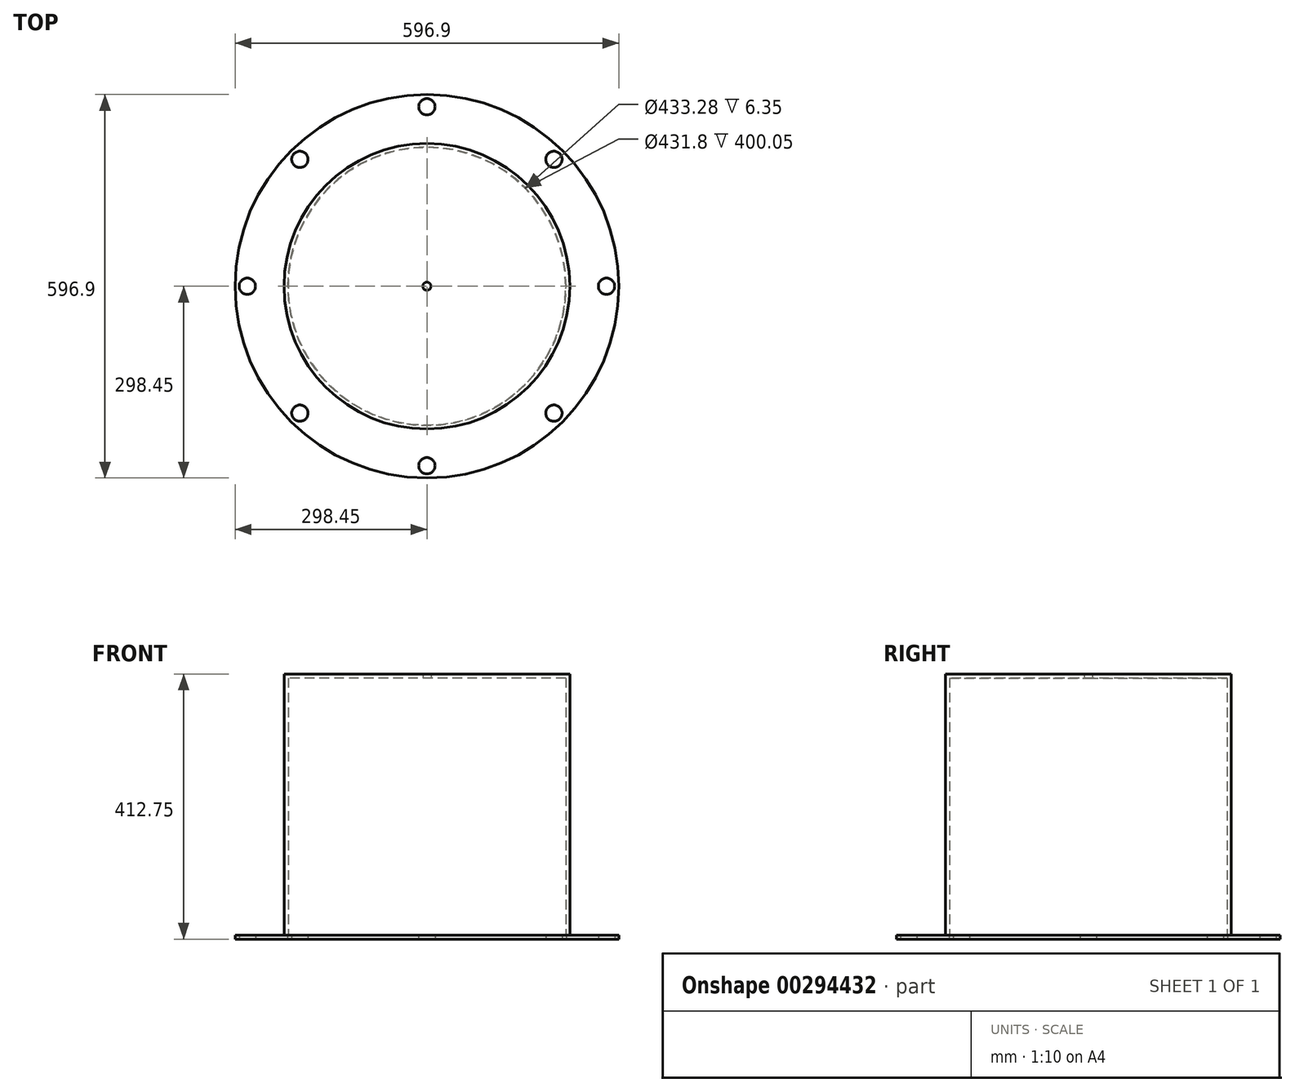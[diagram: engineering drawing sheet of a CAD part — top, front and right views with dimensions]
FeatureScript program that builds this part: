
annotation { "Feature Type Name" : "Feature", "Feature Type Description" : "" }
export const myFeature = defineFeature(function(context is Context, id is Id, definition is map)
    precondition{}
    {
        {
            var Q0;
            Q0=qCreatedBy(makeId("Top.planeOp"),FACE);
            var sketch = newSketch(context, id + "F0", { "sketchPlane" : qUnion([Q0])});
            skCircle(sketch, "E0", {"center": v(0, 0) * mm, "radius": 298.45 * mm});
            skCircle(sketch, "E1", {"center": v(0, 0) * mm, "radius": 216.64 * mm});
            skCircle(sketch, "E2", {"center": v(0, 279.4) * mm, "radius": 12.7 * mm});
            skCircle(sketch, "E3.1.0", {"center": v(-197.57, 197.57) * mm, "radius": 12.7 * mm});
            skCircle(sketch, "E3.2.0", {"center": v(-279.4, 0) * mm, "radius": 12.7 * mm});
            skCircle(sketch, "E3.3.0", {"center": v(-197.57, -197.57) * mm, "radius": 12.7 * mm});
            skCircle(sketch, "E3.4.0", {"center": v(0, -279.4) * mm, "radius": 12.7 * mm});
            skCircle(sketch, "E3.5.0", {"center": v(197.57, -197.57) * mm, "radius": 12.7 * mm});
            skCircle(sketch, "E3.6.0", {"center": v(279.4, 0) * mm, "radius": 12.7 * mm});
            skCircle(sketch, "E3.7.0", {"center": v(197.57, 197.57) * mm, "radius": 12.7 * mm});
            skSolve(sketch);
        }
        {
            var Q0;
            Q0=makeQuery(id+"F0.imprint","IMPRINT",FACE,{"disambiguationData":[TD([[makeQuery(id+"F0.imprint","IMPRINT",EDGE,{"derivedFrom":sQuery(id+"F0.wireOp",EDGE,"E0")}),1.0]])]});
            extrude(context, id + "F1", {"entities" : qUnion([Q0]), "depth" : 6.35 * mm});
        }
        {
            var Q0;
            Q0=makeQuery(id+"F1.opExtrude","CAP_FACE",FACE,{"disambiguationData":[OSD([sQuery(id+"F0.wireOp",EDGE,"E0"),sQuery(id+"F0.wireOp",EDGE,"E1"),sQuery(id+"F0.wireOp",EDGE,"E2"),sQuery(id+"F0.wireOp",EDGE,"E3.1.0"),sQuery(id+"F0.wireOp",EDGE,"E3.2.0"),sQuery(id+"F0.wireOp",EDGE,"E3.3.0"),sQuery(id+"F0.wireOp",EDGE,"E3.4.0"),sQuery(id+"F0.wireOp",EDGE,"E3.5.0"),sQuery(id+"F0.wireOp",EDGE,"E3.6.0"),sQuery(id+"F0.wireOp",EDGE,"E3.7.0")])],"isStart":false});
            cPlane(context, id + "F2", {"entities" : qUnion([Q0]), "cplaneType" : CPlaneType.OFFSET, "offset" : 0 * mm, "width" : 152.4 * mm, "height" : 152.4 * mm});
        }
        {
            var Q0;
            Q0=qCreatedBy(id+"F2.planeOp",FACE);
            var sketch = newSketch(context, id + "F3", { "sketchPlane" : qUnion([Q0])});
            skCircle(sketch, "E4", {"center": v(0, 0) * mm, "radius": 215.9 * mm});
            skCircle(sketch, "E5", {"center": v(0, 0) * mm, "radius": 222.25 * mm});
            skSolve(sketch);
        }
        {
            var Q0;
            Q0=makeQuery(id+"F3.imprint","IMPRINT",FACE,{"disambiguationData":[TD([[makeQuery(id+"F3.imprint","IMPRINT",EDGE,{"derivedFrom":sQuery(id+"F3.wireOp",EDGE,"E4")}),-1.0]])]});
            extrude(context, id + "F4", {"entities" : qUnion([Q0]), "operationType" : NewBodyOperationType.ADD, "depth" : 400.05 * mm});
        }
        {
            var Q0;
            Q0=makeQuery(id+"F4.opExtrude","CAP_FACE",FACE,{"disambiguationData":[OSD([sQuery(id+"F3.wireOp",EDGE,"E4"),sQuery(id+"F3.wireOp",EDGE,"E5")])],"isStart":false});
            cPlane(context, id + "F5", {"entities" : qUnion([Q0]), "cplaneType" : CPlaneType.OFFSET, "offset" : 0 * mm, "width" : 152.4 * mm, "height" : 152.4 * mm});
        }
        {
            var Q0;
            Q0=qCreatedBy(id+"F5.planeOp",FACE);
            var sketch = newSketch(context, id + "F6", { "sketchPlane" : qUnion([Q0])});
            skCircle(sketch, "E6", {"center": v(0, 0) * mm, "radius": 222.25 * mm});
            skCircle(sketch, "E7", {"center": v(0, 0) * mm, "radius": 6.35 * mm});
            skSolve(sketch);
        }
        {
            var Q0;
            Q0=makeQuery(id+"F6.imprint","IMPRINT",FACE,{"disambiguationData":[TD([[makeQuery(id+"F6.imprint","IMPRINT",EDGE,{"derivedFrom":sQuery(id+"F6.wireOp",EDGE,"E6")}),1.0]])]});
            extrude(context, id + "F7", {"entities" : qUnion([Q0]), "operationType" : NewBodyOperationType.ADD, "depth" : 6.35 * mm});
        }
    });
